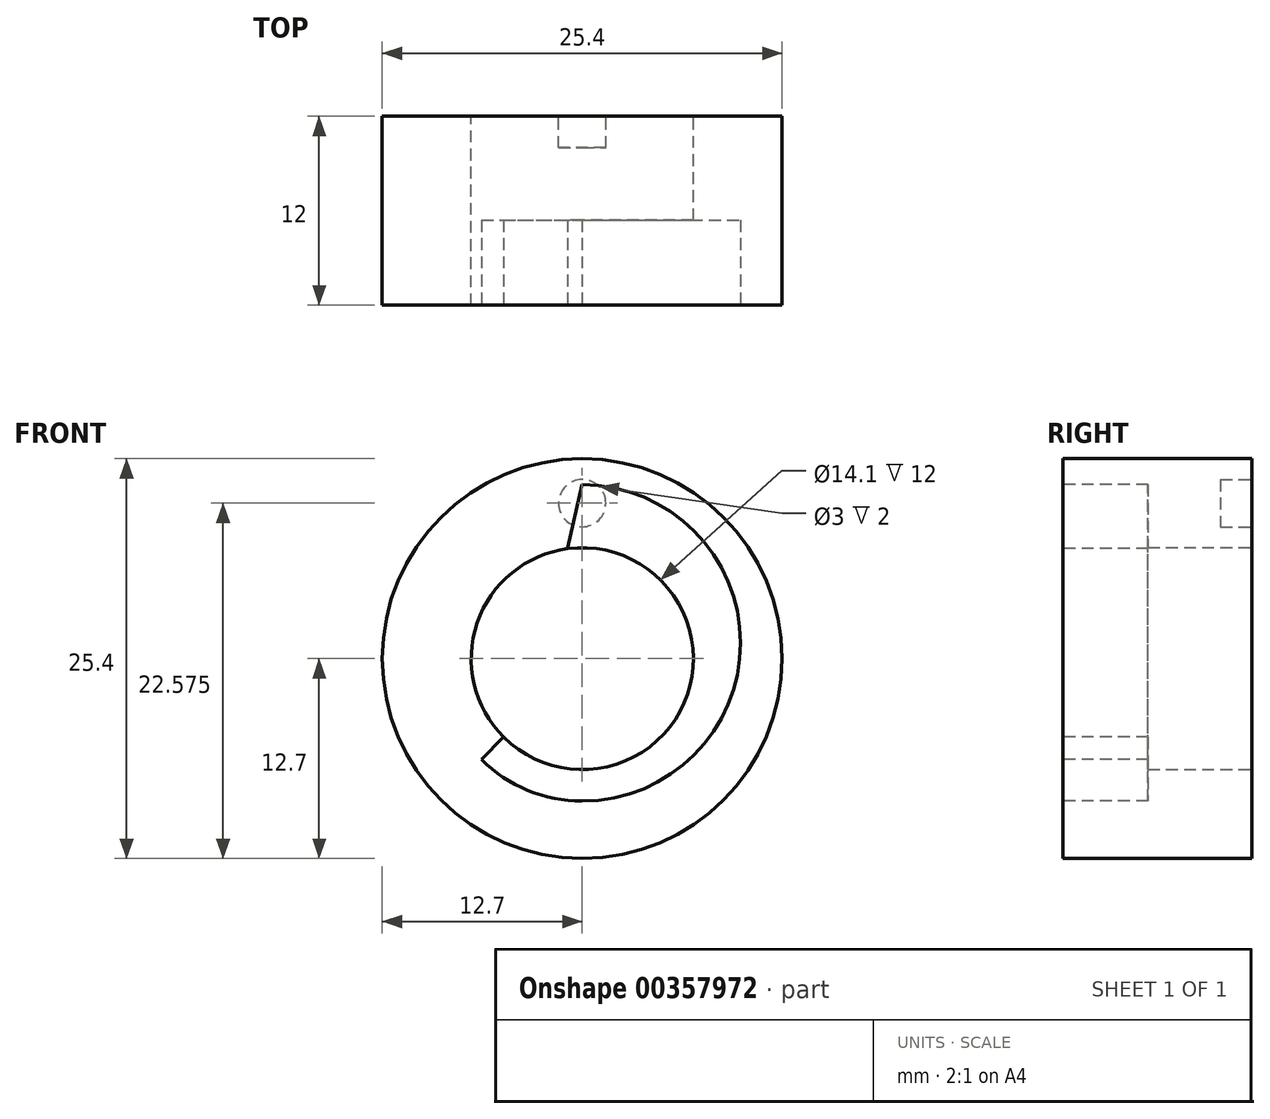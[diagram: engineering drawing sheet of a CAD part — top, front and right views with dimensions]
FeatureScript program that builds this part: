
annotation { "Feature Type Name" : "Feature", "Feature Type Description" : "" }
export const myFeature = defineFeature(function(context is Context, id is Id, definition is map)
    precondition{}
    {
        {
            var Q0;
            Q0=qCreatedBy(makeId("Front.planeOp"),FACE);
            var sketch = newSketch(context, id + "F0", { "sketchPlane" : qUnion([Q0])});
            skCircle(sketch, "E0", {"center": v(0, 0) * mm, "radius": 12.7 * mm});
            skCircle(sketch, "E1", {"center": v(0, 0) * mm, "radius": 7.05 * mm});
            skSolve(sketch);
        }
        {
            var Q0;
            Q0 = qSketchRegion(id + "F0", true);
            extrude(context, id + "F1", {"entities" : qUnion([Q0]), "depth" : 12 * mm});
        }
        {
            var Q0;
            Q0=makeQuery(id+"F1.opExtrude","CAP_FACE",FACE,{"disambiguationData":[OSD([sQuery(id+"F0.wireOp",EDGE,"E0"),sQuery(id+"F0.wireOp",EDGE,"E1")])],"isStart":false});
            var sketch = newSketch(context, id + "F2", { "sketchPlane" : qUnion([Q0])});
            skLineSegment(sketch, "E2", {"start": v(0, 7.05) * mm, "end": v(0, 9.05) * mm, "construction": true});
            skLineSegment(sketch, "E3", {"start": v(0, 9.05) * mm, "end": v(0, 11.05) * mm, "construction": true});
            skArc(sketch, "E4", {"start": v(-6.4, -6.4) * mm, "mid": v(-3.46, -8.36) * mm, "end": v(0, -9.05) * mm});
            skArc(sketch, "E5", {"start": v(0, -9.05) * mm, "mid": v(10.05, 1) * mm, "end": v(0, 11.05) * mm});
            skPoint(sketch, "E5.startSnap0", {"position": v(0, 10.05) * mm});
            skLineSegment(sketch, "E6", {"start": v(0, 0) * mm, "end": v(-6.4, -6.4) * mm, "construction": true});
            skLineSegment(sketch, "E7", {"start": v(-6.4, -6.4) * mm, "end": v(-4.99, -4.99) * mm});
            skArc(sketch, "E8", {"start": v(-4.99, -4.99) * mm, "mid": v(6.68, -2.27) * mm, "end": v(-0.92, 6.99) * mm});
            skLineSegment(sketch, "E9", {"start": v(0, 11.05) * mm, "end": v(4.34, 10.06) * mm, "construction": true});
            skLineSegment(sketch, "E10", {"start": v(0, 11.05) * mm, "end": v(-0.92, 6.99) * mm});
            skSolve(sketch);
        }
        {
            var Q0;
            Q0 = qSketchRegion(id + "F2", true);
            extrude(context, id + "F3", {"entities" : qUnion([Q0]), "operationType" : NewBodyOperationType.REMOVE, "oppositeDirection" : true, "depth" : 5.4 * mm});
        }
        {
            var Q0;
            Q0=makeQuery(id+"F1.opExtrude","CAP_FACE",FACE,{"disambiguationData":[OSD([sQuery(id+"F0.wireOp",EDGE,"E0"),sQuery(id+"F0.wireOp",EDGE,"E1")])],"isStart":true});
            var sketch = newSketch(context, id + "F4", { "sketchPlane" : qUnion([Q0])});
            skLineSegment(sketch, "E11", {"start": v(0, 7.05) * mm, "end": v(0, 12.7) * mm, "construction": true});
            skCircle(sketch, "E12", {"center": v(0, 9.88) * mm, "radius": 1.5 * mm});
            skSolve(sketch);
        }
        {
            var Q0;
            Q0 = qSketchRegion(id + "F4", true);
            extrude(context, id + "F5", {"entities" : qUnion([Q0]), "operationType" : NewBodyOperationType.REMOVE, "oppositeDirection" : true, "depth" : 2 * mm});
        }
    });
